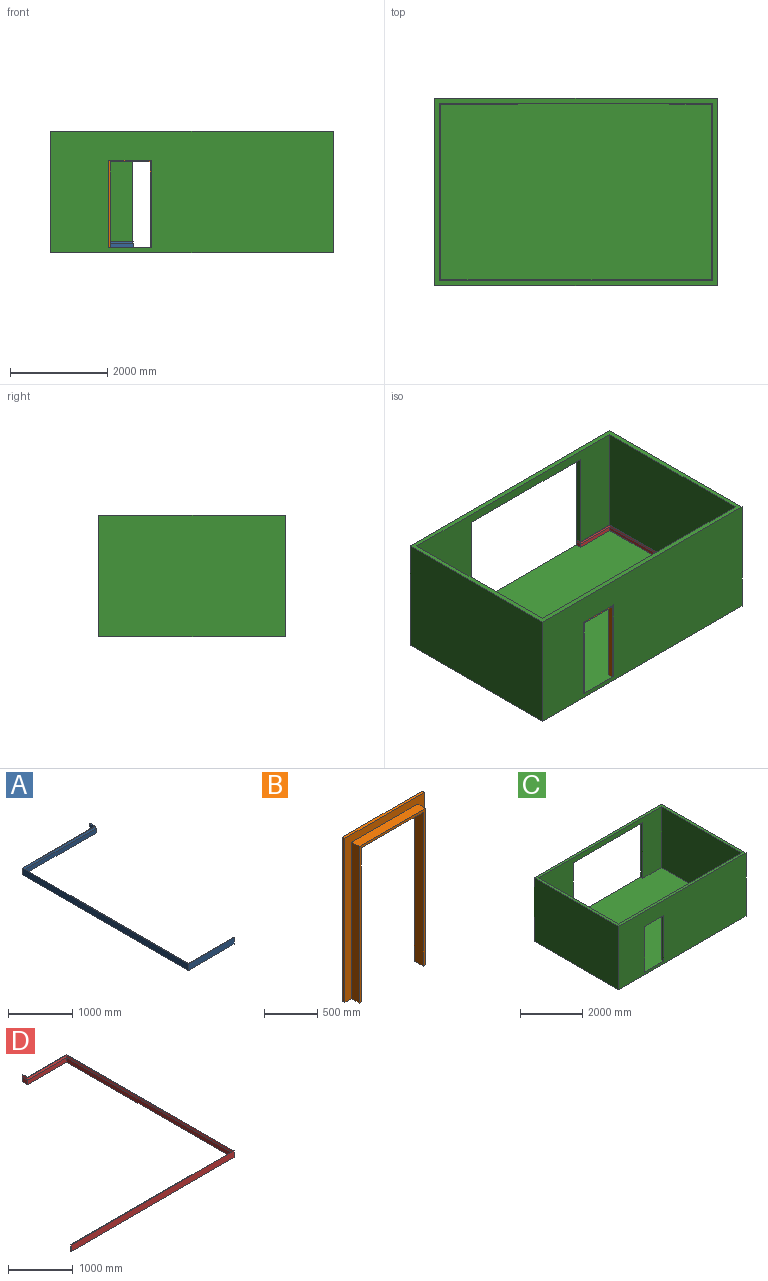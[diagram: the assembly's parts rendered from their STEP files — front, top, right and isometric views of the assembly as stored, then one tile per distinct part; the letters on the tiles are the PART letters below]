
ASSEMBLY  parts=4 mates=4
PART A: 16 faces, bbox 1610x3750x125 mm
  f0: plane 125x20mm, normal (0,1,0), area 2300mm2, adj f2,f3,f4,f12,f15
  f1: plane 125x20mm, normal (1,0,0), area 2300mm2, adj f11,f12,f13,f14,f15
  f2: plane 125x100mm, normal (-1,0,0), area 12500mm2, adj f0,f7,f12,f15
  f3: plane 120x40mm, normal (0.97,0,0.24), area 4741.6mm2, adj f0,f4,f6,f12
  f4: plane 120x85mm, normal (1,0,0), area 10200mm2, adj f0,f3,f5,f15
  f5: plane 1590x85mm, normal (0,-1,0), area 135150mm2, adj f4,f6,f10,f15
  f6: plane 1600x40mm, normal (0,-0.97,0.24), area 65557.4mm2, adj f3,f5,f9,f12
  f7: plane 1590x125mm, normal (0,1,0), area 198750mm2, adj f2,f8,f12,f15
  f8: plane 3650x125mm, normal (-1,0,0), area 456250mm2, adj f7,f11,f12,f15
  f9: plane 3630x40mm, normal (0.97,0,0.24), area 149256.4mm2, adj f6,f10,f12,f13
  f10: plane 3610x85mm, normal (1,0,0), area 306850mm2, adj f5,f9,f14,f15
  f11: plane 1005.18x125mm, normal (0,-1,0), area 125647.3mm2, adj f1,f8,f12,f15
  f12: plane 3750x1600mm, normal (0,0,1), area 63351.8mm2, adj f0,f1,f2,f3,f6,f7,f8,f9
  f13: plane 995.18x40mm, normal (0,0.97,0.24), area 40826.1mm2, adj f1,f9,f12,f14
  f14: plane 985.18x85mm, normal (0,1,0), area 83740.2mm2, adj f1,f10,f13,f15
  f15: plane 3750x1610mm, normal (0,0,-1), area 126503.6mm2, adj f0,f1,f2,f4,f5,f7,f8,f10
PART B: 17 faces, bbox 1060x130x1890 mm
  f0: plane 130x120mm, normal (0,0,-1), area 5799.5mm2, adj f2,f3,f4,f5,f11,f13,f15
  f1: plane 130x120mm, normal (0,0,-1), area 5799.5mm2, adj f10,f11,f12,f13,f14,f15,f16
  f2: plane 1770x115mm, normal (1,0,0), area 203550mm2, adj f0,f5,f9,f15
  f3: plane 1800x100mm, normal (-1,0,0), area 180000mm2, adj f0,f8,f13,f15
  f4: plane 1890x30mm, normal (-1,0,0), area 56700mm2, adj f0,f7,f11,f13
  f5: plane 1876.73x106.73mm, normal (0.14,0.99,0), area 196521.3mm2, adj f0,f2,f6,f11
  f6: plane 1033.46x106.73mm, normal (0,0.99,-0.14), area 99882.5mm2, adj f5,f9,f10,f11
  f7: plane 1060x30mm, normal (0,0,1), area 31800mm2, adj f4,f11,f12,f13
  f8: plane 880x100mm, normal (0,0,1), area 88000mm2, adj f3,f13,f14,f15
  f9: plane 820x115mm, normal (0,0,-1), area 94300mm2, adj f2,f6,f15,f16
  f10: plane 1876.73x106.73mm, normal (-0.14,0.99,0), area 196521.3mm2, adj f1,f6,f11,f16
  f11: plane 1890x1060mm, normal (0,1,0), area 63872mm2, adj f0,f1,f4,f5,f6,f7,f10,f12
  f12: plane 1890x30mm, normal (1,0,0), area 56700mm2, adj f1,f7,f11,f13
  f13: plane 1890x1060mm, normal (0,-1,0), area 419400mm2, adj f0,f1,f3,f4,f7,f8,f12,f14
  f14: plane 1800x100mm, normal (1,0,0), area 180000mm2, adj f1,f8,f13,f15
  f15: plane 1800x880mm, normal (0,-1,0), area 132600mm2, adj f0,f1,f2,f3,f8,f9,f14,f16
  f16: plane 1770x115mm, normal (-1,0,0), area 203550mm2, adj f1,f9,f10,f15
PART C: 17 faces, bbox 5820x3850x2500 mm
  f0: plane 5820x2500mm, normal (0,-1,0), area 12966000mm2, adj f1,f3,f4,f5,f10,f11,f12,f13
  f1: plane 5820x3850mm, normal (0,0,1), area 1894000mm2, adj f0,f2,f3,f4,f6,f7,f8,f9
  f2: plane 5820x2500mm, normal (0,1,0), area 7576000mm2, adj f1,f3,f4,f5,f10,f14,f15,f16
  f3: plane 3850x2500mm, normal (-1,0,0), area 9625000mm2, adj f0,f1,f2,f5
  f4: plane 3850x2500mm, normal (1,0,0), area 9625000mm2, adj f0,f1,f2,f5
  f5: plane 5820x3850mm, normal (0,0,-1), area 22407000mm2, adj f0,f2,f3,f4
  f6: plane 5620x2400mm, normal (0,-1,0), area 6514000mm2, adj f1,f7,f9,f10,f14,f15,f16
  f7: plane 3650x2400mm, normal (1,0,0), area 8760000mm2, adj f1,f6,f8,f10
  f8: plane 5620x2400mm, normal (0,1,0), area 11904000mm2, adj f1,f7,f9,f10,f11,f12,f13
  f9: plane 3650x2400mm, normal (-1,0,0), area 8760000mm2, adj f1,f6,f8,f10
  f10: plane 5620x3850mm, normal (0,0,1), area 20918000mm2, adj f0,f2,f6,f7,f8,f9,f11,f12
  f11: plane 1800x100mm, normal (1,0,0), area 180000mm2, adj f0,f8,f10,f13
  f12: plane 1800x100mm, normal (-1,0,0), area 180000mm2, adj f0,f8,f10,f13
  f13: plane 880x100mm, normal (0,0,-1), area 88000mm2, adj f0,f8,f11,f12
  f14: plane 2200x100mm, normal (-1,0,0), area 220000mm2, adj f2,f6,f10,f15
  f15: plane 3170x100mm, normal (0,0,-1), area 317000mm2, adj f2,f6,f14,f16
  f16: plane 2200x100mm, normal (1,0,0), area 220000mm2, adj f2,f6,f10,f15
PART D: 16 faces, bbox 3555.6x3750x125 mm
  f0: plane 125x20mm, normal (0,1,0), area 2300mm2, adj f2,f3,f4,f12,f13
  f1: plane 125x20mm, normal (-1,0,0), area 2300mm2, adj f11,f12,f13,f14,f15
  f2: plane 125x100mm, normal (1,0,0), area 12500mm2, adj f0,f7,f12,f13
  f3: plane 120x85mm, normal (-1,0,0), area 10200mm2, adj f0,f4,f6,f13
  f4: plane 120x40mm, normal (-0.97,0,0.24), area 4741.6mm2, adj f0,f3,f5,f12
  f5: plane 870x40mm, normal (0,-0.97,0.24), area 35458.7mm2, adj f4,f6,f10,f12
  f6: plane 860x85mm, normal (0,-1,0), area 73100mm2, adj f3,f5,f9,f13
  f7: plane 860x125mm, normal (0,1,0), area 107500mm2, adj f2,f8,f12,f13
  f8: plane 3650x125mm, normal (1,0,0), area 456250mm2, adj f7,f11,f12,f13
  f9: plane 3610x85mm, normal (-1,0,0), area 306850mm2, adj f6,f10,f13,f14
  f10: plane 3630x40mm, normal (-0.97,0,0.24), area 149256.4mm2, adj f5,f9,f12,f15
  f11: plane 3555.6x125mm, normal (0,-1,0), area 444450.4mm2, adj f1,f8,f12,f13
  f12: plane 3750x3555.6mm, normal (0,0,1), area 81556mm2, adj f0,f1,f2,f4,f5,f7,f8,f10
  f13: plane 3750x3555.6mm, normal (0,0,-1), area 162912.1mm2, adj f0,f1,f2,f3,f6,f7,f8,f9
  f14: plane 3535.6x85mm, normal (0,1,0), area 300526.3mm2, adj f1,f9,f13,f15
  f15: plane 3545.6x40mm, normal (0,0.97,0.24), area 145982.8mm2, adj f1,f10,f12,f14
PLACE A t=(-0.18,0,0)mm
PLACE B t=(-835.17,-1845.53,0)mm
PLACE C t=(-0.17,-20.53,-100)mm
PLACE D at identity
MATE fastened D.f13 <-> C.f10  axis (0,0,1) through (2809.83,-1845.53,0)mm
MATE planar B.f13 <-> C.f8  axis (0,-1,0) through (-1275.17,-1845.53,1890)mm
MATE fastened A.f15 <-> B.f0  axis (0,0,-1) through (-1805.17,-1845.53,0)mm
MATE fastened C.f13 <-> B.f8  axis (0,0,-1) through (-1275.17,-1895.53,1800)mm
